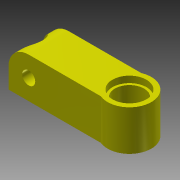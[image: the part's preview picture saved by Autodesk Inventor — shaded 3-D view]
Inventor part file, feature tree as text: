
AUTODESK INVENTOR PART (.ipt)
format: ipt  version: 2013 (Build 170138000, 138)  size: 168,448 bytes
history: native  units: mm
features: extrude x10, sketch x10, chamfer x1
ambient origin geometry x8: Origin, YZ Plane, XZ Plane, XY Plane, X Axis, Y Axis, Z Axis, Center Point
bodies: Solid1 (feature_tree)
feature tree (21):
  extrude  "Extrusion1"  Depth=50.0mm
  extrude  "Extrusion2"  Depth=25.0mm TaperAngle=0.0deg
  extrude  "Extrusion3"  Depth=25.0mm TaperAngle=0.0deg
  extrude  "Extrusion4"  Depth=73.0mm TaperAngle=0.0deg
  extrude  "Extrusion15"  Depth=4.0mm TaperAngle=0.0deg
  extrude  "Extrusion16"  Depth=1.5mm TaperAngle=45.0deg
  chamfer  "Chamfer2"  Distance=10.0mm
  extrude  "Extrusion17"  Depth=5.5mm TaperAngle=0.0deg
  extrude  "Extrusion19"  Depth=5.5mm TaperAngle=0.0deg
  extrude  "Extrusion20"  [1 undecoded]
  extrude  "Extrusion21"  [1 undecoded]
  sketch  "Sketch1"  dims[d0=12.5mm d2=50.0mm]
  sketch  "Sketch2"  dims[d3=25.0mm d4=0.0mm d5=25.0mm d6=0.0mm]
  sketch  "Sketch3"  dims[d7=8.1mm d9=25.0mm d10=0.0mm]
  sketch  "Sketch4"  dims[d11=18.1mm d13=73.0mm d14=0.0mm]
  sketch  "Sketch17"  dims[d78=21.1mm d80=4.0mm d81=0.0mm]
  sketch  "Sketch19"  dims[d82=4.0mm d83=0.0mm d84=1.5mm d85=2.0mm d86=45.0deg]
  sketch  "Sketch20"  dims[d87=3.0mm d88=10.0mm d89=0.0mm]
  sketch  "Sketch22"  dims[d94=17.0mm d96=5.5mm d97=0.0mm]
  sketch  "Sketch23"  dims[d98=13.2mm d99=5.5mm d100=0.0mm]
  sketch  "Sketch24"  dims[d101=10.0mm d102=0.0mm]
note: 2 required parameter values undecoded (feature->parameter linkage not recoverable at this tier; creation-order binding heuristic only, values carry confidence <= 0.55)
